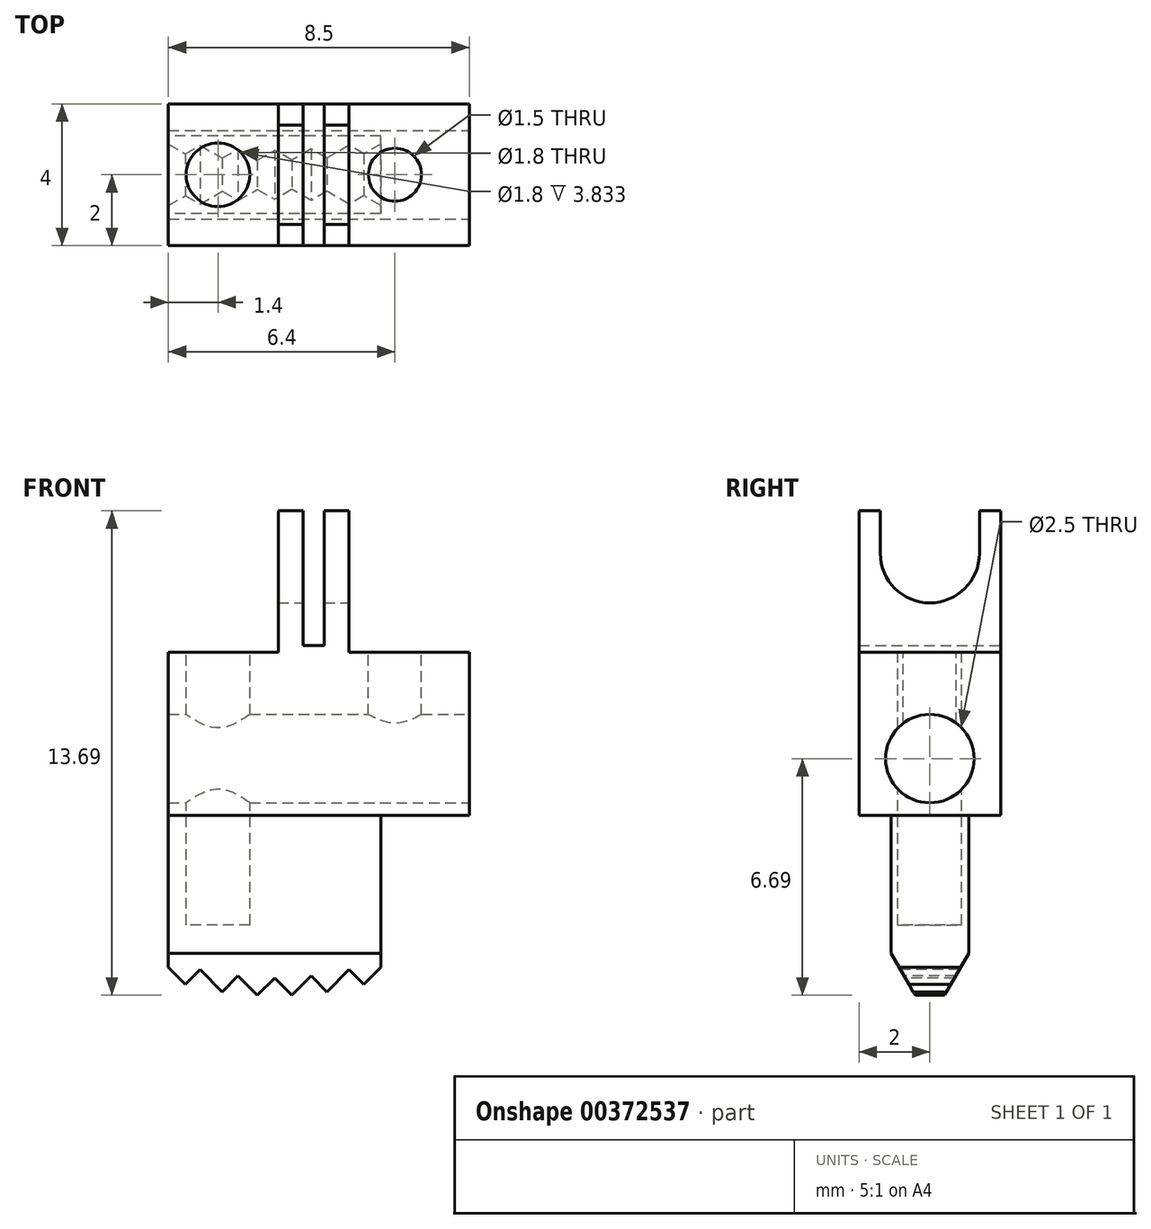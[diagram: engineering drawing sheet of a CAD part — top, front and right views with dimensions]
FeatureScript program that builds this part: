
annotation { "Feature Type Name" : "Feature", "Feature Type Description" : "" }
export const myFeature = defineFeature(function(context is Context, id is Id, definition is map)
    precondition{}
    {
        {
            var Q0;
            Q0=qCreatedBy(makeId("Front.planeOp"),FACE);
            var sketch = newSketch(context, id + "F0", { "sketchPlane" : qUnion([Q0])});
            skLineSegment(sketch, "E0", {"start": v(0, 0) * mm, "end": v(-6, 0) * mm});
            skLineSegment(sketch, "E1", {"start": v(0, 0) * mm, "end": v(0, 5.1) * mm});
            skLineSegment(sketch, "E2", {"start": v(0, 5.1) * mm, "end": v(2.5, 5.1) * mm});
            skLineSegment(sketch, "E3", {"start": v(2.5, 5.1) * mm, "end": v(2.5, 9.7) * mm});
            skLineSegment(sketch, "E4", {"start": v(2.5, 9.7) * mm, "end": v(-0.9, 9.7) * mm});
            skLineSegment(sketch, "E5", {"start": v(-0.9, 9.7) * mm, "end": v(-0.9, 13.7) * mm});
            skLineSegment(sketch, "E6", {"start": v(-0.9, 13.7) * mm, "end": v(-1.6, 13.7) * mm});
            skLineSegment(sketch, "E7", {"start": v(-1.6, 13.7) * mm, "end": v(-1.6, 9.9) * mm});
            skLineSegment(sketch, "E8", {"start": v(-1.6, 9.9) * mm, "end": v(-2.2, 9.9) * mm});
            skLineSegment(sketch, "E9", {"start": v(-2.2, 9.9) * mm, "end": v(-2.2, 13.7) * mm});
            skLineSegment(sketch, "E10", {"start": v(-2.2, 13.7) * mm, "end": v(-2.9, 13.7) * mm});
            skLineSegment(sketch, "E11", {"start": v(-2.9, 13.7) * mm, "end": v(-2.9, 9.7) * mm});
            skLineSegment(sketch, "E12", {"start": v(-2.9, 9.7) * mm, "end": v(-6, 9.7) * mm});
            skLineSegment(sketch, "E13", {"start": v(-6, 9.7) * mm, "end": v(-6, 0) * mm});
            skLineSegment(sketch, "E14", {"start": v(-3, 0) * mm, "end": v(-3, 10) * mm, "construction": true});
            skCircle(sketch, "E15", {"center": v(-3, 10) * mm, "radius": 10 * mm, "construction": true});
            skLineSegment(sketch, "E16", {"start": v(0, 5.1) * mm, "end": v(-6, 5.1) * mm});
            skSolve(sketch);
        }
        {
            var Q0;
            Q0=makeQuery(id+"F0.imprint","IMPRINT",FACE,{"disambiguationData":[TD([[makeQuery(id+"F0.imprint","IMPRINT",EDGE,{"derivedFrom":sQuery(id+"F0.wireOp",EDGE,"E2")}),1.0]])]});
            extrude(context, id + "F1", {"entities" : qUnion([Q0]), "endBound" : BoundingType.SYMMETRIC, "depth" : 4 * mm});
        }
        {
            var Q0;
            {var subQ2=sQuery(id+"F0.wireOp",EDGE,"E0");Q0=makeQuery(id+"F0.imprint","IMPRINT",FACE,{"disambiguationData":[TD([[makeQuery(id+"F0.imprint","IMPRINT",EDGE,{"derivedFrom":subQ2}),-1.0]])]});}
            extrude(context, id + "F2", {"entities" : qUnion([Q0]), "operationType" : NewBodyOperationType.ADD, "endBound" : BoundingType.SYMMETRIC, "depth" : 2.2 * mm});
        }
        {
            var Q0;
            Q0=makeQuery(id+"F1.opExtrude","SWEPT_FACE",FACE,{"disambiguationData":[OSD([sQuery(id+"F0.wireOp",EDGE,"E5")])]});
            var sketch = newSketch(context, id + "F3", { "sketchPlane" : qUnion([Q0])});
            skLineSegment(sketch, "E17", {"start": v(2, 11.1) * mm, "end": v(-2, 11.1) * mm, "construction": true});
            skArc(sketch, "E18", {"start": v(-1.4, 12.5) * mm, "mid": v(0, 11.1) * mm, "end": v(1.4, 12.5) * mm});
            skLineSegment(sketch, "E19", {"start": v(-1.4, 12.5) * mm, "end": v(-1.4, 13.9) * mm});
            skLineSegment(sketch, "E20", {"start": v(-1.4, 13.9) * mm, "end": v(1.4, 13.9) * mm});
            skLineSegment(sketch, "E21", {"start": v(1.4, 13.9) * mm, "end": v(1.4, 12.5) * mm});
            skSolve(sketch);
        }
        {
            var Q0;
            {var subQ5=sQuery(id+"F3.wireOp",EDGE,"E20");Q0=makeQuery(id+"F3.imprint","IMPRINT",FACE,{"disambiguationData":[TD([[makeQuery(id+"F3.imprint","IMPRINT",EDGE,{"derivedFrom":subQ5}),-1.0]])]});}
            var Q1;
            {var subQ5=sQuery(id+"F3.wireOp",EDGE,"E18");Q1=makeQuery(id+"F3.imprint","IMPRINT",FACE,{"disambiguationData":[TD([[makeQuery(id+"F3.imprint","IMPRINT",EDGE,{"derivedFrom":subQ5}),1.0]])]});}
            extrude(context, id + "F4", {"entities" : qUnion([Q0, Q1]), "operationType" : NewBodyOperationType.REMOVE, "oppositeDirection" : true, "depth" : 2 * mm});
        }
        {
            var Q0;
            Q0=makeQuery(id+"F1.opExtrude","SWEPT_FACE",FACE,{"disambiguationData":[OSD([sQuery(id+"F0.wireOp",EDGE,"E3")])]});
            var sketch = newSketch(context, id + "F5", { "sketchPlane" : qUnion([Q0])});
            skLineSegment(sketch, "E22", {"start": v(0, 9.7) * mm, "end": v(0, 6.7) * mm, "construction": true});
            skCircle(sketch, "E23", {"center": v(0, 6.7) * mm, "radius": 1.25 * mm});
            skSolve(sketch);
        }
        {
            var Q0;
            Q0=makeQuery(id+"F5.imprint","IMPRINT",FACE,{"disambiguationData":[TD([[makeQuery(id+"F5.imprint","IMPRINT",EDGE,{"derivedFrom":sQuery(id+"F5.wireOp",EDGE,"E23")}),1.0]])]});
            extrude(context, id + "F6", {"entities" : qUnion([Q0]), "operationType" : NewBodyOperationType.REMOVE, "oppositeDirection" : true, "depth" : 8.5 * mm});
        }
        {
            var Q0;
            Q0=makeQuery(id+"F1.opExtrude","SWEPT_FACE",FACE,{"disambiguationData":[OSD([sQuery(id+"F0.wireOp",EDGE,"E4")])]});
            var sketch = newSketch(context, id + "F7", { "sketchPlane" : qUnion([Q0])});
            skCircle(sketch, "E24", {"center": v(0.4, 0) * mm, "radius": 0.75 * mm});
            skSolve(sketch);
        }
        {
            var Q0;
            Q0=makeQuery(id+"F7.imprint","IMPRINT",FACE,{"disambiguationData":[TD([[makeQuery(id+"F7.imprint","IMPRINT",EDGE,{"derivedFrom":sQuery(id+"F7.wireOp",EDGE,"E24")}),1.0]])]});
            extrude(context, id + "F8", {"entities" : qUnion([Q0]), "operationType" : NewBodyOperationType.REMOVE, "oppositeDirection" : true, "depth" : 3 * mm});
        }
        {
            var Q0;
            Q0=makeQuery(id+"F1.opExtrude","SWEPT_FACE",FACE,{"disambiguationData":[OSD([sQuery(id+"F0.wireOp",EDGE,"E12")])]});
            var sketch = newSketch(context, id + "F9", { "sketchPlane" : qUnion([Q0])});
            skLineSegment(sketch, "E25", {"start": v(-4.6, 2) * mm, "end": v(-4.6, -2) * mm, "construction": true});
            skCircle(sketch, "E26", {"center": v(-4.6, 0) * mm, "radius": 0.9 * mm});
            skSolve(sketch);
        }
        {
            var Q0;
            Q0=makeQuery(id+"F9.imprint","IMPRINT",FACE,{"disambiguationData":[TD([[makeQuery(id+"F9.imprint","IMPRINT",EDGE,{"derivedFrom":sQuery(id+"F9.wireOp",EDGE,"E26")}),1.0]])]});
            extrude(context, id + "F10", {"entities" : qUnion([Q0]), "operationType" : NewBodyOperationType.REMOVE, "oppositeDirection" : true, "depth" : 7.7 * mm});
        }
        {
            var Q0;
            Q0=makeQuery(id+"F2.opExtrude","CAP_EDGE",EDGE,{"disambiguationData":[OSD([sQuery(id+"F0.wireOp",EDGE,"E0")])],"isStart":false});
            var Q1;
            Q1=makeQuery(id+"F2.opExtrude","CAP_EDGE",EDGE,{"disambiguationData":[OSD([sQuery(id+"F0.wireOp",EDGE,"E0")])],"isStart":true});
            chamfer(context, id + "F11", {"entities" : qUnion([Q0, Q1]), "chamferType" : ChamferType.OFFSET_ANGLE, "width" : 1.2 * mm, "oppositeDirection" : true, "angle" : 30 * degree, "tangentPropagation" : true});
        }
        {
            var Q0;
            Q0=qCreatedBy(makeId("Front.planeOp"),FACE);
            var sketch = newSketch(context, id + "F12", { "sketchPlane" : qUnion([Q0])});
            skCircle(sketch, "E27", {"center": v(-3, 10) * mm, "radius": 10 * mm, "construction": true});
            skPoint(sketch, "E28", {"position": v(-3, 0) * mm});
            skCircle(sketch, "E29", {"center": v(-3, 10) * mm, "radius": 9.5 * mm, "construction": true});
            skLineSegment(sketch, "E30", {"start": v(-3, 0.5) * mm, "end": v(-3.49, 0.01) * mm});
            skLineSegment(sketch, "E31", {"start": v(-3, 0.5) * mm, "end": v(-2.51, 0.01) * mm});
            skLineSegment(sketch, "E32", {"start": v(-3.49, 0.01) * mm, "end": v(-4.03, 0.56) * mm});
            skLineSegment(sketch, "E33", {"start": v(-4.03, 0.56) * mm, "end": v(-4.48, 0.1) * mm});
            skLineSegment(sketch, "E34", {"start": v(-4.48, 0.1) * mm, "end": v(-5.1, 0.74) * mm});
            skLineSegment(sketch, "E35", {"start": v(-5.1, 0.74) * mm, "end": v(-5.52, 0.32) * mm});
            skLineSegment(sketch, "E36", {"start": v(-5.52, 0.32) * mm, "end": v(-6, 0.8) * mm});
            skLineSegment(sketch, "E37", {"start": v(-6, 0.8) * mm, "end": v(-6, 0) * mm});
            skLineSegment(sketch, "E38", {"start": v(-6, 0) * mm, "end": v(0, 0) * mm});
            skLineSegment(sketch, "E39", {"start": v(0, 0) * mm, "end": v(0, 0.8) * mm});
            skLineSegment(sketch, "E40", {"start": v(-2.51, 0.01) * mm, "end": v(-1.97, 0.56) * mm});
            skLineSegment(sketch, "E41", {"start": v(-1.97, 0.56) * mm, "end": v(-1.52, 0.1) * mm});
            skLineSegment(sketch, "E42", {"start": v(-1.52, 0.1) * mm, "end": v(-0.9, 0.74) * mm});
            skLineSegment(sketch, "E43", {"start": v(-0.9, 0.74) * mm, "end": v(-0.48, 0.32) * mm});
            skLineSegment(sketch, "E44", {"start": v(-0.48, 0.32) * mm, "end": v(0, 0.8) * mm});
            skSolve(sketch);
        }
        {
            var Q0;
            Q0=makeQuery(id+"F12.imprint","IMPRINT",FACE,{"disambiguationData":[TD([[makeQuery(id+"F12.imprint","IMPRINT",EDGE,{"derivedFrom":sQuery(id+"F12.wireOp",EDGE,"E30")}),1.0]])]});
            extrude(context, id + "F13", {"entities" : qUnion([Q0]), "operationType" : NewBodyOperationType.REMOVE, "endBound" : BoundingType.SYMMETRIC, "oppositeDirection" : true, "depth" : 25 * mm});
        }
    });
